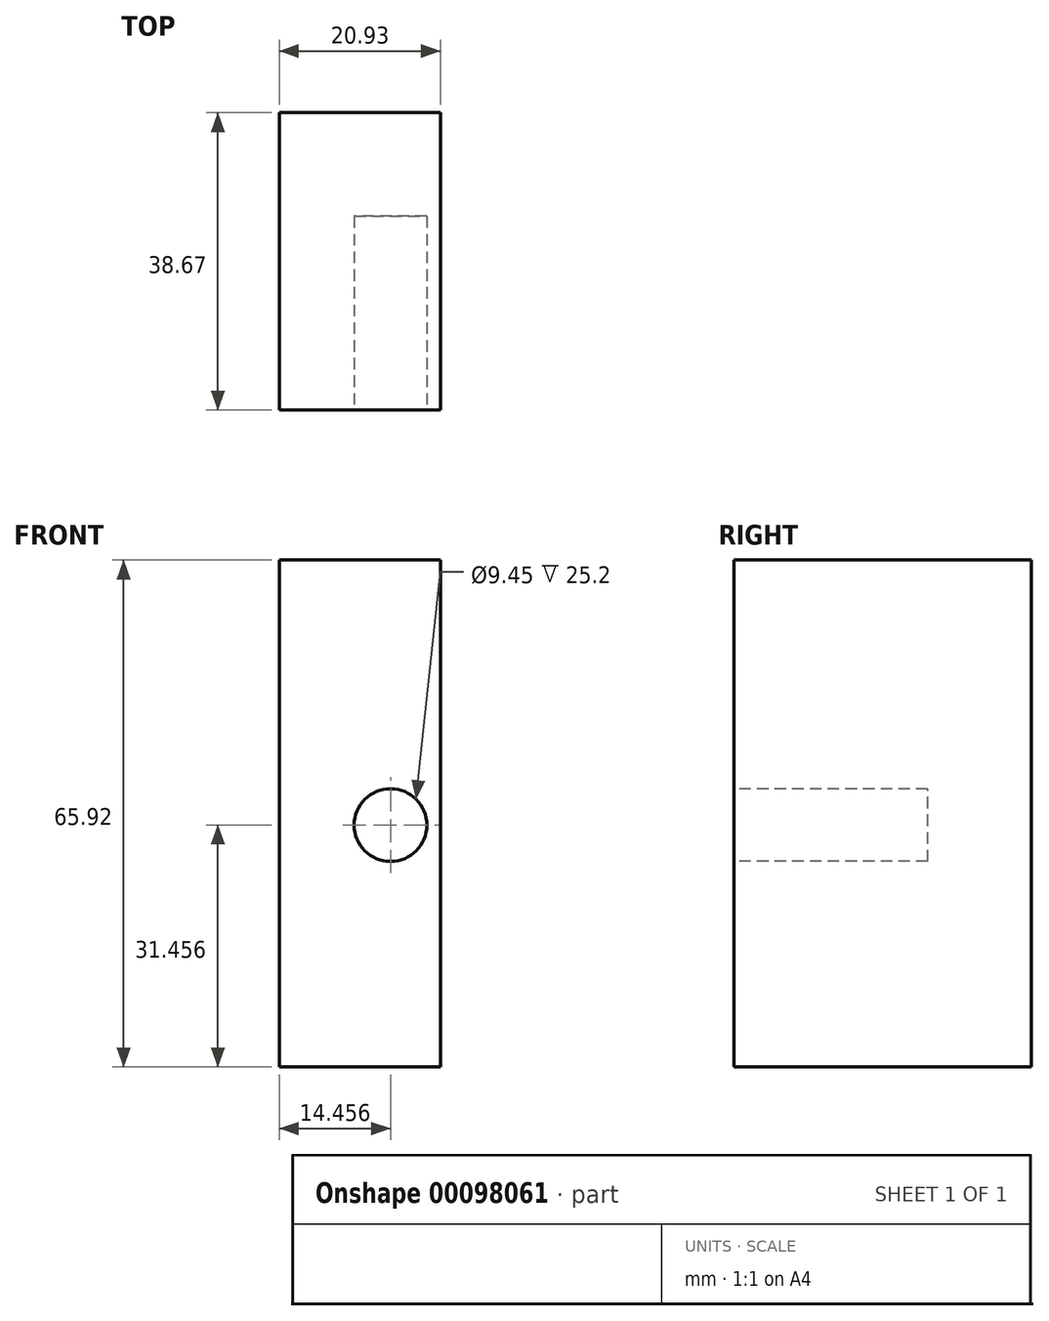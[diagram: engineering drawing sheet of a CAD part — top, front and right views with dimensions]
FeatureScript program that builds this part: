
annotation { "Feature Type Name" : "Feature", "Feature Type Description" : "" }
export const myFeature = defineFeature(function(context is Context, id is Id, definition is map)
    precondition{}
    {
        {
            var Q0;
            Q0=qCreatedBy(makeId("Front.planeOp"),FACE);
            var sketch = newSketch(context, id + "F0", { "sketchPlane" : qUnion([Q0])});
            skLineSegment(sketch, "E0.bottom", {"start": v(-39.47, 25.78) * mm, "end": v(-18.54, 25.78) * mm});
            skLineSegment(sketch, "E0.top", {"start": v(-39.47, 12.9) * mm, "end": v(-18.54, 12.9) * mm});
            skLineSegment(sketch, "E0.left", {"start": v(-39.47, 25.78) * mm, "end": v(-39.47, 12.9) * mm});
            skLineSegment(sketch, "E0.right", {"start": v(-18.54, 25.78) * mm, "end": v(-18.54, 12.9) * mm});
            skSolve(sketch);
        }
        {
            var Q0;
            Q0=makeQuery(id+"F0.imprint","IMPRINT",FACE,{"disambiguationData":[TD([[makeQuery(id+"F0.imprint","IMPRINT",EDGE,{"derivedFrom":sQuery(id+"F0.wireOp",EDGE,"E0.bottom")}),-1.0]])]});
            extrude(context, id + "F1", {"entities" : qUnion([Q0]), "depth" : 38.67 * mm});
        }
        {
            var Q0;
            Q0=makeQuery(id+"F1.opExtrude","SWEPT_FACE",FACE,{"disambiguationData":[OSD([sQuery(id+"F0.wireOp",EDGE,"E0.bottom")])]});
            extrude(context, id + "F2", {"entities" : qUnion([Q0]), "operationType" : NewBodyOperationType.ADD, "depth" : 53.04 * mm});
        }
        {
            var Q0;
            {var subQ0=sQuery(id+"F0.wireOp",EDGE,"E0.bottom");Q0=makeQuery(id+"F2.boolean.opBoolean","MERGE",FACE,{"derivedFrom":[makeQuery(id+"F1.opExtrude","CAP_FACE",FACE,{"disambiguationData":[OSD([subQ0,sQuery(id+"F0.wireOp",EDGE,"E0.top"),sQuery(id+"F0.wireOp",EDGE,"E0.left"),sQuery(id+"F0.wireOp",EDGE,"E0.right")])],"isStart":false}),makeQuery(id+"F2.opExtrude","SWEPT_FACE",FACE,{"disambiguationData":[OSD([subQ0]),TDD([makeQuery(id+"F1.opExtrude","CAP_EDGE",EDGE,{"disambiguationData":[OSD([subQ0])],"isStart":false})])]})]});}
            var sketch = newSketch(context, id + "F3", { "sketchPlane" : qUnion([Q0])});
            skCircle(sketch, "E1", {"center": v(-25.01, 44.35) * mm, "radius": 4.73 * mm});
            skSolve(sketch);
        }
        {
            var Q0;
            Q0=makeQuery(id+"F3.imprint","IMPRINT",FACE,{"disambiguationData":[TD([[makeQuery(id+"F3.imprint","IMPRINT",EDGE,{"derivedFrom":sQuery(id+"F3.wireOp",EDGE,"E1")}),1.0]])]});
            extrude(context, id + "F4", {"entities" : qUnion([Q0]), "operationType" : NewBodyOperationType.REMOVE, "oppositeDirection" : true, "depth" : 25.2 * mm});
        }
    });
